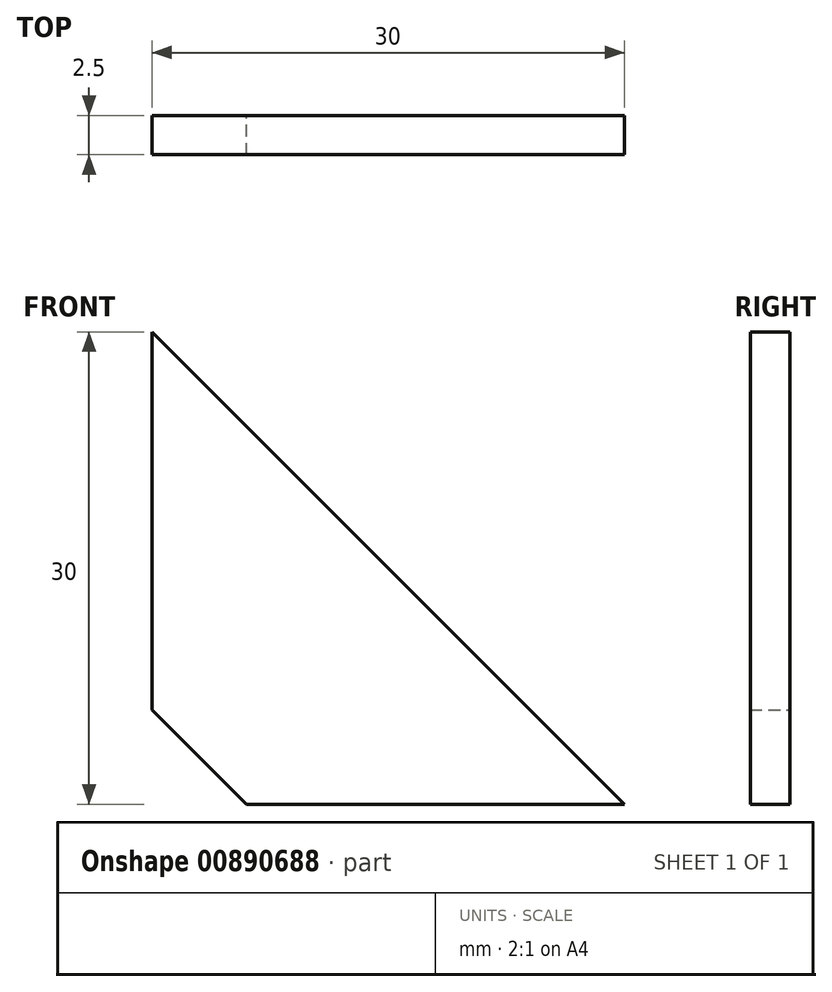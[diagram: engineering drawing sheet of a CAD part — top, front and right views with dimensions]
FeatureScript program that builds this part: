
annotation { "Feature Type Name" : "Feature", "Feature Type Description" : "" }
export const myFeature = defineFeature(function(context is Context, id is Id, definition is map)
    precondition{}
    {
        {
            var Q0;
            Q0=qCreatedBy(makeId("Front.planeOp"),FACE);
            var sketch = newSketch(context, id + "F0", { "sketchPlane" : qUnion([Q0])});
            skLineSegment(sketch, "E0.bottom", {"start": v(0, 0) * mm, "end": v(30, 0) * mm, "construction": true});
            skLineSegment(sketch, "E0.top", {"start": v(0, 30) * mm, "end": v(30, 30) * mm, "construction": true});
            skLineSegment(sketch, "E0.left", {"start": v(0, 0) * mm, "end": v(0, 30) * mm, "construction": true});
            skLineSegment(sketch, "E0.right", {"start": v(30, 0) * mm, "end": v(30, 30) * mm, "construction": true});
            skLineSegment(sketch, "E1.bottom", {"start": v(0, 0) * mm, "end": v(6, 0) * mm, "construction": true});
            skLineSegment(sketch, "E1.top", {"start": v(0, 6) * mm, "end": v(6, 6) * mm, "construction": true});
            skLineSegment(sketch, "E1.left", {"start": v(0, 0) * mm, "end": v(0, 6) * mm, "construction": true});
            skLineSegment(sketch, "E1.right", {"start": v(6, 0) * mm, "end": v(6, 6) * mm, "construction": true});
            skLineSegment(sketch, "E2", {"start": v(0, 30) * mm, "end": v(0, 6) * mm});
            skLineSegment(sketch, "E3", {"start": v(6, 0) * mm, "end": v(30, 0) * mm});
            skLineSegment(sketch, "E4", {"start": v(0, 30) * mm, "end": v(30, 0) * mm});
            skLineSegment(sketch, "E5", {"start": v(6, 0) * mm, "end": v(0, 6) * mm});
            skSolve(sketch);
        }
        {
            var Q0;
            Q0 = qSketchRegion(id + "F0", true);
            extrude(context, id + "F1", {"entities" : qUnion([Q0]), "depth" : 2.5 * mm, "offsetDistance" : 25 * mm});
        }
    });
